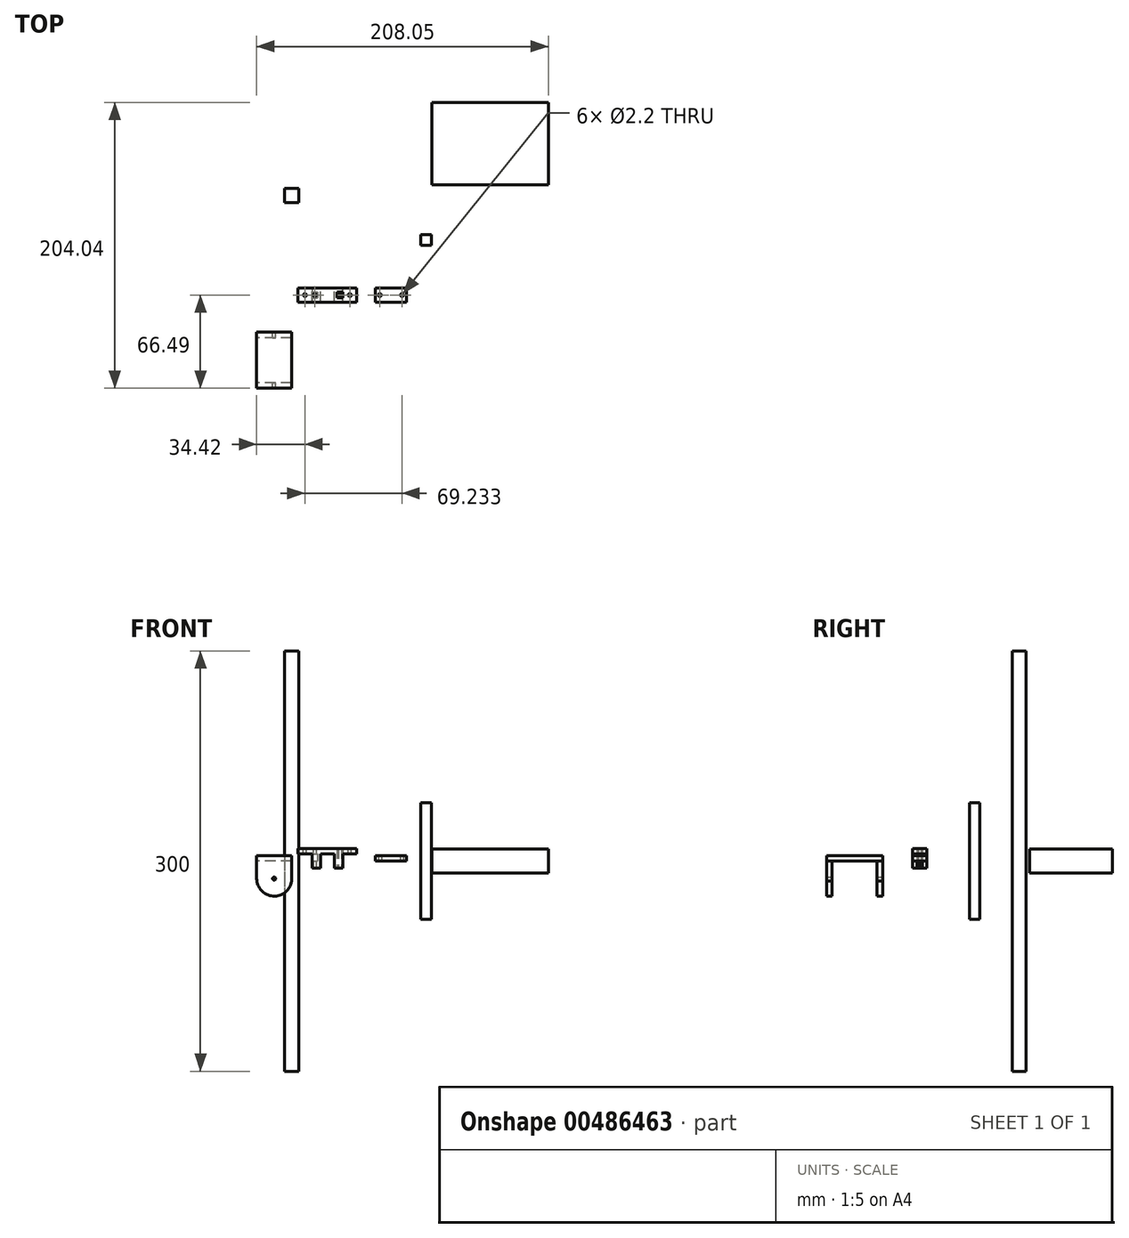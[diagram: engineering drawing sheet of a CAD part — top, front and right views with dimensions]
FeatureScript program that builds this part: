
annotation { "Feature Type Name" : "Feature", "Feature Type Description" : "" }
export const myFeature = defineFeature(function(context is Context, id is Id, definition is map)
    precondition{}
    {
        {
            assignVariable(context, id + "F0", {"name" : "top_length", "anyValue" : 10});
        }
        {
            assignVariable(context, id + "F1", {"name" : "protrude_length", "anyValue" : 10});
        }
        {
            var Q0;
            Q0=qCreatedBy(makeId("Front.planeOp"),FACE);
            var sketch = newSketch(context, id + "F2", { "sketchPlane" : qUnion([Q0])});
            skLineSegment(sketch, "E0.bottom", {"start": v(5, 5) * mm, "end": v(-5, 5) * mm, "construction": true});
            skLineSegment(sketch, "E0.top", {"start": v(5, -5) * mm, "end": v(-5, -5) * mm, "construction": true});
            skLineSegment(sketch, "E0.left", {"start": v(5, 5) * mm, "end": v(5, -5) * mm, "construction": true});
            skLineSegment(sketch, "E0.right", {"start": v(-5, 5) * mm, "end": v(-5, -5) * mm, "construction": true});
            skPoint(sketch, "E0.middle", {"position": v(0, 0) * mm});
            skLineSegment(sketch, "E1", {"start": v(-5, -4.9) * mm, "end": v(-5, 5) * mm});
            skLineSegment(sketch, "E2", {"start": v(-5, 5) * mm, "end": v(5, 5) * mm});
            skLineSegment(sketch, "E3", {"start": v(5, 5) * mm, "end": v(5, -4.9) * mm});
            skLineSegment(sketch, "E4", {"start": v(-5, -4.9) * mm, "end": v(-11, -4.9) * mm});
            skLineSegment(sketch, "E5", {"start": v(5, -4.9) * mm, "end": v(11, -4.9) * mm});
            skLineSegment(sketch, "E6", {"start": v(11, -4.9) * mm, "end": v(11, 9) * mm});
            skLineSegment(sketch, "E7", {"start": v(11, 9) * mm, "end": v(-11, 9) * mm});
            skLineSegment(sketch, "E8", {"start": v(-11, -4.9) * mm, "end": v(-11, 9) * mm});
            skSolve(sketch);
        }
        {
            var Q0;
            Q0 = qSketchRegion(id + "F2", true);
            extrude(context, id + "F3", {"entities" : qUnion([Q0]), "depth" : (getVariable(context, 'top_length')) * mm, "symmetric" : true});
        }
        {
            var Q0;
            Q0=makeQuery(id+"F3.opExtrude","SWEPT_FACE",FACE,{"disambiguationData":[OSD([sQuery(id+"F2.wireOp",EDGE,"E4")])]});
            var sketch = newSketch(context, id + "F4", { "sketchPlane" : qUnion([Q0])});
            skCircle(sketch, "E9", {"center": v(-9, 0) * mm, "radius": 1.1 * mm});
            skCircle(sketch, "E10.MirrorC", {"center": v(9, 0) * mm, "radius": 1.1 * mm});
            skLineSegment(sketch, "E11.bottom", {"start": v(-11, -2) * mm, "end": v(-7, -2) * mm});
            skLineSegment(sketch, "E11.top", {"start": v(-11, 2) * mm, "end": v(-7, 2) * mm});
            skLineSegment(sketch, "E11.left", {"start": v(-11, -2) * mm, "end": v(-11, 2) * mm});
            skLineSegment(sketch, "E11.right", {"start": v(-7, -2) * mm, "end": v(-7, 2) * mm});
            skLineSegment(sketch, "E12.MirrorCS", {"start": v(11, 2) * mm, "end": v(7, 2) * mm});
            skLineSegment(sketch, "E13.MirrorCS", {"start": v(11, -2) * mm, "end": v(11, 2) * mm});
            skLineSegment(sketch, "E14.MirrorCS", {"start": v(11, -2) * mm, "end": v(7, -2) * mm});
            skLineSegment(sketch, "E15.MirrorCS", {"start": v(7, -2) * mm, "end": v(7, 2) * mm});
            skSolve(sketch);
        }
        {
            var Q0;
            Q0=makeQuery(id+"F4.imprint","IMPRINT",FACE,{"disambiguationData":[TD([[makeQuery(id+"F4.imprint","IMPRINT",EDGE,{"derivedFrom":sQuery(id+"F4.wireOp",EDGE,"E9")}),1.0]])]});
            var Q1;
            Q1=makeQuery(id+"F4.imprint","IMPRINT",FACE,{"disambiguationData":[TD([[makeQuery(id+"F4.imprint","IMPRINT",EDGE,{"derivedFrom":sQuery(id+"F4.wireOp",EDGE,"E10.MirrorC")}),-1.0]])]});
            extrude(context, id + "F5", {"entities" : qUnion([Q0, Q1]), "operationType" : NewBodyOperationType.REMOVE, "endBound" : BoundingType.THROUGH_ALL, "oppositeDirection" : true, "depth" : 25 * mm});
        }
        {
            var Q0;
            Q0 = qSketchRegion(id + "F4", true);
            extrude(context, id + "F6", {"entities" : qUnion([Q0]), "operationType" : NewBodyOperationType.REMOVE, "oppositeDirection" : true, "depth" : 10 * mm, "hasSecondDirection" : true, "secondDirectionOppositeDirection" : false, "secondDirectionDepth" : -5 * mm});
        }
        {
            var Q0;
            Q0=qCreatedBy(makeId("Top.planeOp"),FACE);
            var sketch = newSketch(context, id + "F7", { "sketchPlane" : qUnion([Q0])});
            skLineSegment(sketch, "E16.bottom", {"start": v(34.33, -5) * mm, "end": v(56.33, -5) * mm});
            skLineSegment(sketch, "E16.top", {"start": v(34.33, 5) * mm, "end": v(56.33, 5) * mm});
            skLineSegment(sketch, "E16.left", {"start": v(34.33, -5) * mm, "end": v(34.33, 5) * mm});
            skLineSegment(sketch, "E16.right", {"start": v(56.33, -5) * mm, "end": v(56.33, 5) * mm});
            skPoint(sketch, "E16.middle", {"position": v(45.33, 0) * mm});
            skSolve(sketch);
        }
        {
            var Q0;
            Q0=makeQuery(id+"F7.imprint","IMPRINT",FACE,{"disambiguationData":[TD([[makeQuery(id+"F7.imprint","IMPRINT",EDGE,{"derivedFrom":sQuery(id+"F7.wireOp",EDGE,"E16.bottom")}),1.0]])]});
            extrude(context, id + "F8", {"entities" : qUnion([Q0]), "depth" : 4 * mm});
        }
        {
            var Q0;
            Q0=makeQuery(id+"F3.opExtrude","SWEPT_FACE",FACE,{"disambiguationData":[OSD([sQuery(id+"F2.wireOp",EDGE,"E8")])]});
            var sketch = newSketch(context, id + "F9", { "sketchPlane" : qUnion([Q0])});
            skLineSegment(sketch, "E17.bottom", {"start": v(-5, 9) * mm, "end": v(5, 9) * mm});
            skLineSegment(sketch, "E17.top", {"start": v(-5, 5) * mm, "end": v(5, 5) * mm});
            skLineSegment(sketch, "E17.left", {"start": v(-5, 9) * mm, "end": v(-5, 5) * mm});
            skLineSegment(sketch, "E17.right", {"start": v(5, 9) * mm, "end": v(5, 5) * mm});
            skSolve(sketch);
        }
        {
            var Q0;
            Q0=makeQuery(id+"F3.opExtrude","SWEPT_FACE",FACE,{"disambiguationData":[OSD([sQuery(id+"F2.wireOp",EDGE,"E6")])]});
            var sketch = newSketch(context, id + "F10", { "sketchPlane" : qUnion([Q0])});
            skLineSegment(sketch, "E18.bottom", {"start": v(-5, 9) * mm, "end": v(5, 9) * mm});
            skLineSegment(sketch, "E18.top", {"start": v(-5, 5) * mm, "end": v(5, 5) * mm});
            skLineSegment(sketch, "E18.left", {"start": v(-5, 9) * mm, "end": v(-5, 5) * mm});
            skLineSegment(sketch, "E18.right", {"start": v(5, 9) * mm, "end": v(5, 5) * mm});
            skSolve(sketch);
        }
        {
            var Q0;
            Q0 = qSketchRegion(id + "F9", true);
            extrude(context, id + "F11", {"entities" : qUnion([Q0]), "operationType" : NewBodyOperationType.ADD, "depth" : (getVariable(context, 'protrude_length')) * mm});
        }
        {
            var Q0;
            Q0 = qSketchRegion(id + "F10", true);
            extrude(context, id + "F12", {"entities" : qUnion([Q0]), "operationType" : NewBodyOperationType.ADD, "depth" : (getVariable(context, 'protrude_length')) * mm});
        }
        {
            var Q0;
            Q0=qCreatedBy(makeId("Top.planeOp"),FACE);
            var sketch = newSketch(context, id + "F13", { "sketchPlane" : qUnion([Q0])});
            skLineSegment(sketch, "E19.bottom", {"start": v(-50.42, -26.49) * mm, "end": v(-25.42, -26.49) * mm});
            skLineSegment(sketch, "E19.top", {"start": v(-50.42, -66.49) * mm, "end": v(-25.42, -66.49) * mm});
            skLineSegment(sketch, "E19.left", {"start": v(-50.42, -26.49) * mm, "end": v(-50.42, -66.49) * mm});
            skLineSegment(sketch, "E19.right", {"start": v(-25.42, -26.49) * mm, "end": v(-25.42, -66.49) * mm});
            skSolve(sketch);
        }
        {
            var Q0;
            Q0=makeQuery(id+"F13.imprint","IMPRINT",FACE,{"disambiguationData":[TD([[makeQuery(id+"F13.imprint","IMPRINT",EDGE,{"derivedFrom":sQuery(id+"F13.wireOp",EDGE,"E19.bottom")}),-1.0]])]});
            extrude(context, id + "F14", {"entities" : qUnion([Q0]), "depth" : 4 * mm});
        }
        {
            var Q0;
            Q0=makeQuery(id+"F14.opExtrude","SWEPT_FACE",FACE,{"disambiguationData":[OSD([sQuery(id+"F13.wireOp",EDGE,"E19.bottom")])]});
            var sketch = newSketch(context, id + "F15", { "sketchPlane" : qUnion([Q0])});
            skLineSegment(sketch, "E20", {"start": v(37.92, 4) * mm, "end": v(37.92, -35.46) * mm, "construction": true});
            skLineSegment(sketch, "E21", {"start": v(50.42, 4) * mm, "end": v(50.42, -35.46) * mm, "construction": true});
            skCircle(sketch, "E22", {"center": v(37.92, -12.5) * mm, "radius": 12.5 * mm, "construction": true});
            skLineSegment(sketch, "E23", {"start": v(50.42, 4) * mm, "end": v(50.42, -12.5) * mm});
            skLineSegment(sketch, "E24", {"start": v(25.42, 4) * mm, "end": v(25.54, -14.26) * mm});
            skArc(sketch, "E25", {"start": v(25.54, -14.26) * mm, "mid": v(38.8, -24.97) * mm, "end": v(50.42, -12.5) * mm});
            skSolve(sketch);
        }
        {
            var Q0;
            {var subQ3=sQuery(id+"F15.wireOp",EDGE,"E25");Q0=makeQuery(id+"F15.imprint","IMPRINT",FACE,{"disambiguationData":[TD([[makeQuery(id+"F15.imprint","IMPRINT",EDGE,{"derivedFrom":subQ3}),1.0]])]});}
            extrude(context, id + "F16", {"entities" : qUnion([Q0]), "operationType" : NewBodyOperationType.ADD, "oppositeDirection" : true, "depth" : 40 * mm});
        }
        {
            var Q0;
            Q0=makeQuery(id+"F16.boolean.opBoolean","MERGE",FACE,{"derivedFrom":[makeQuery(id+"F14.opExtrude","SWEPT_FACE",FACE,{"disambiguationData":[OSD([sQuery(id+"F13.wireOp",EDGE,"E19.left")])]}),makeQuery(id+"F16.opExtrude","SWEPT_FACE",FACE,{"disambiguationData":[OSD([sQuery(id+"F15.wireOp",EDGE,"E23")])]})]});
            var sketch = newSketch(context, id + "F17", { "sketchPlane" : qUnion([Q0])});
            skLineSegment(sketch, "E26.bottom", {"start": v(30.49, 0) * mm, "end": v(62.49, 0) * mm});
            skLineSegment(sketch, "E26.top", {"start": v(30.49, -40) * mm, "end": v(62.49, -40) * mm});
            skLineSegment(sketch, "E26.left", {"start": v(30.49, 0) * mm, "end": v(30.49, -40) * mm});
            skLineSegment(sketch, "E26.right", {"start": v(62.49, 0) * mm, "end": v(62.49, -40) * mm});
            skSolve(sketch);
        }
        {
            var Q0;
            Q0 = qSketchRegion(id + "F17", true);
            extrude(context, id + "F18", {"entities" : qUnion([Q0]), "operationType" : NewBodyOperationType.REMOVE, "oppositeDirection" : true, "depth" : 25 * mm});
        }
        {
            var Q0;
            Q0=qCreatedBy(makeId("Top.planeOp"),FACE);
            var sketch = newSketch(context, id + "F19", { "sketchPlane" : qUnion([Q0])});
            skLineSegment(sketch, "E27.bottom", {"start": v(-20.48, 76) * mm, "end": v(-30.48, 76) * mm});
            skLineSegment(sketch, "E27.top", {"start": v(-20.48, 66) * mm, "end": v(-30.48, 66) * mm});
            skLineSegment(sketch, "E27.left", {"start": v(-20.48, 76) * mm, "end": v(-20.48, 66) * mm});
            skLineSegment(sketch, "E27.right", {"start": v(-30.48, 76) * mm, "end": v(-30.48, 66) * mm});
            skSolve(sketch);
        }
        {
            var Q0;
            Q0=makeQuery(id+"F19.imprint","IMPRINT",FACE,{"disambiguationData":[TD([[makeQuery(id+"F19.imprint","IMPRINT",EDGE,{"derivedFrom":sQuery(id+"F19.wireOp",EDGE,"E27.bottom")}),1.0]])]});
            extrude(context, id + "F20", {"entities" : qUnion([Q0]), "depth" : 300 * mm, "symmetric" : true});
        }
        {
            var Q0;
            {var subQ0=sQuery(id+"F13.wireOp",EDGE,"E19.bottom");Q0=makeQuery(id+"F16.boolean.opBoolean","MERGE",FACE,{"derivedFrom":[makeQuery(id+"F14.opExtrude","SWEPT_FACE",FACE,{"disambiguationData":[OSD([subQ0])]}),makeQuery(id+"F16.opExtrude","CAP_FACE",FACE,{"disambiguationData":[OSD([subQ0,sQuery(id+"F15.wireOp",EDGE,"E23"),sQuery(id+"F15.wireOp",EDGE,"E24"),sQuery(id+"F15.wireOp",EDGE,"E25")])],"isStart":true})]});}
            var sketch = newSketch(context, id + "F21", { "sketchPlane" : qUnion([Q0])});
            skCircle(sketch, "E28", {"center": v(37.92, -12.5) * mm, "radius": 1.1 * mm});
            skSolve(sketch);
        }
        {
            var Q0;
            Q0 = qSketchRegion(id + "F21", true);
            extrude(context, id + "F22", {"entities" : qUnion([Q0]), "operationType" : NewBodyOperationType.REMOVE, "endBound" : BoundingType.THROUGH_ALL, "oppositeDirection" : true, "depth" : 25 * mm});
        }
        {
            var Q0;
            Q0=makeQuery(id+"F11.boolean.opBoolean","MERGE",FACE,{"derivedFrom":[makeQuery(id+"F3.opExtrude","SWEPT_FACE",FACE,{"disambiguationData":[OSD([sQuery(id+"F2.wireOp",EDGE,"E7")])]}),makeQuery(id+"F11.opExtrude","SWEPT_FACE",FACE,{"disambiguationData":[OSD([sQuery(id+"F9.wireOp",EDGE,"E17.bottom")])]})]});
            var sketch = newSketch(context, id + "F23", { "sketchPlane" : qUnion([Q0])});
            skCircle(sketch, "E29", {"center": v(-16, 0) * mm, "radius": 1.1 * mm});
            skCircle(sketch, "E30.MirrorC", {"center": v(16, 0) * mm, "radius": 1.1 * mm});
            skSolve(sketch);
        }
        {
            var Q0;
            Q0 = qSketchRegion(id + "F23", true);
            extrude(context, id + "F24", {"entities" : qUnion([Q0]), "operationType" : NewBodyOperationType.REMOVE, "endBound" : BoundingType.THROUGH_ALL, "oppositeDirection" : true, "depth" : 25 * mm});
        }
        {
            var Q0;
            Q0=qCreatedBy(makeId("Top.planeOp"),FACE);
            var sketch = newSketch(context, id + "F25", { "sketchPlane" : qUnion([Q0])});
            skLineSegment(sketch, "E31.bottom", {"start": v(74.63, 78.55) * mm, "end": v(157.63, 78.55) * mm});
            skLineSegment(sketch, "E31.top", {"start": v(74.63, 137.55) * mm, "end": v(157.63, 137.55) * mm});
            skLineSegment(sketch, "E31.left", {"start": v(74.63, 78.55) * mm, "end": v(74.63, 137.55) * mm});
            skLineSegment(sketch, "E31.right", {"start": v(157.63, 78.55) * mm, "end": v(157.63, 137.55) * mm});
            skSolve(sketch);
        }
        {
            var Q0;
            Q0=makeQuery(id+"F25.imprint","IMPRINT",FACE,{"disambiguationData":[TD([[makeQuery(id+"F25.imprint","IMPRINT",EDGE,{"derivedFrom":sQuery(id+"F25.wireOp",EDGE,"E31.bottom")}),1.0]])]});
            extrude(context, id + "F26", {"entities" : qUnion([Q0]), "depth" : 17 * mm, "symmetric" : true});
        }
        {
            var Q0;
            Q0=makeQuery(id+"F8.opExtrude","CAP_FACE",FACE,{"disambiguationData":[OSD([sQuery(id+"F7.wireOp",EDGE,"E16.bottom"),sQuery(id+"F7.wireOp",EDGE,"E16.top"),sQuery(id+"F7.wireOp",EDGE,"E16.left"),sQuery(id+"F7.wireOp",EDGE,"E16.right")])],"isStart":true});
            var sketch = newSketch(context, id + "F27", { "sketchPlane" : qUnion([Q0])});
            skCircle(sketch, "E32", {"center": v(37.43, 0) * mm, "radius": 1.1 * mm});
            skCircle(sketch, "E33", {"center": v(53.23, 0) * mm, "radius": 1.1 * mm});
            skSolve(sketch);
        }
        {
            var Q0;
            Q0 = qSketchRegion(id + "F27", true);
            extrude(context, id + "F28", {"entities" : qUnion([Q0]), "operationType" : NewBodyOperationType.REMOVE, "endBound" : BoundingType.UP_TO_NEXT, "oppositeDirection" : true, "depth" : 25 * mm});
        }
        {
            var Q0;
            Q0=qCreatedBy(makeId("Top.planeOp"),FACE);
            var sketch = newSketch(context, id + "F29", { "sketchPlane" : qUnion([Q0])});
            skLineSegment(sketch, "E34.bottom", {"start": v(66.64, 35.48) * mm, "end": v(74.14, 35.48) * mm});
            skLineSegment(sketch, "E34.top", {"start": v(66.64, 42.98) * mm, "end": v(74.14, 42.98) * mm});
            skLineSegment(sketch, "E34.left", {"start": v(66.64, 35.48) * mm, "end": v(66.64, 42.98) * mm});
            skLineSegment(sketch, "E34.right", {"start": v(74.14, 35.48) * mm, "end": v(74.14, 42.98) * mm});
            skSolve(sketch);
        }
        {
            var Q0;
            Q0=makeQuery(id+"F29.imprint","IMPRINT",FACE,{"disambiguationData":[TD([[makeQuery(id+"F29.imprint","IMPRINT",EDGE,{"derivedFrom":sQuery(id+"F29.wireOp",EDGE,"E34.bottom")}),1.0]])]});
            extrude(context, id + "F30", {"entities" : qUnion([Q0]), "depth" : 83 * mm, "offsetDistance" : 25 * mm, "symmetric" : true});
        }
    });
